# Revit family: sign_diva_410-8220
name_source: partatom
category: Lighting Fixtures
units: mm (PartAtom-declared; Revit-internal decimal feet)

## family parameters
Cut with Voids When Loaded = No
Host = Face
Light Source = No
Part Type = Normal
Room Calculation Point = No
Round Connector Dimension = Use Diameter
Shared = No

## types (1)
- 410-8220-D01-H27-L00-S27 (1 x LED, 9229.8 lm, 2700K)
    Apparent Load = 68 VA
    CIE Flux Codes = 46 76 93 80 73
    Color Rendering = 1A/90…99
    Color Temperature = 2700K
    Default Elevation = 1800 mm
    Description = SIGN DIVA
    Height = 72 mm
    Lamp = 1 x LED
    Lamp Light Flux = 9229.8 lm
    Lamp count = 1
    Length = 570 mm
    Luminous efficacy = 99 lm/W
    Manufacturer = Prolicht
    ModVariant = No
    Model = 410-8220
    Mounting Place = Ceiling
    Mounting Type = Pendant
    Number of Poles = 1
    OnlyDefault = Yes
    Power Factor = 1
    Product Name = SIGN DIVA
    Product group = Suspended lights
    ProductGroupID = 941
    Protection Class = Protection class
    Protection Degree = Degree of protection
    RLX_Detail_Level = 1
    RLX_Emergency_Light_Flux = 0 lm
    RLX_Emergency_Type = 0
    RLX_Emergency_Type_DB = No
    RlxData = <blob elided: 219181 chars, md5=afdc38ef>
    Socket = socket
    Standby Power = 0 W
    System Light Flux = 6729 lm
    System Power = 68 W
    Type Comments = DIFFUSER Opal (01),LED COLOUR DIR 2700 K (27),SHINE RING ABSICHTLICH_LEER (00),LED COLOUR IND 2700 K (27)
    Type Image = 410-8220.jpg
    URL = http://relux.com
    VarID = 410-8220-d01-h27-l00-s27
    Voltage = 0 V
    Weight = 0.00 kg
    Width = 0 mm  [stored 0 ft]

note: [stored X ft] marks values corroborated as IEEE doubles in the binary element streams (Revit-internal decimal feet)

## geometry (parser evidence)
native form markers: Sweep x14
no freeform markers — native parametric forms only
